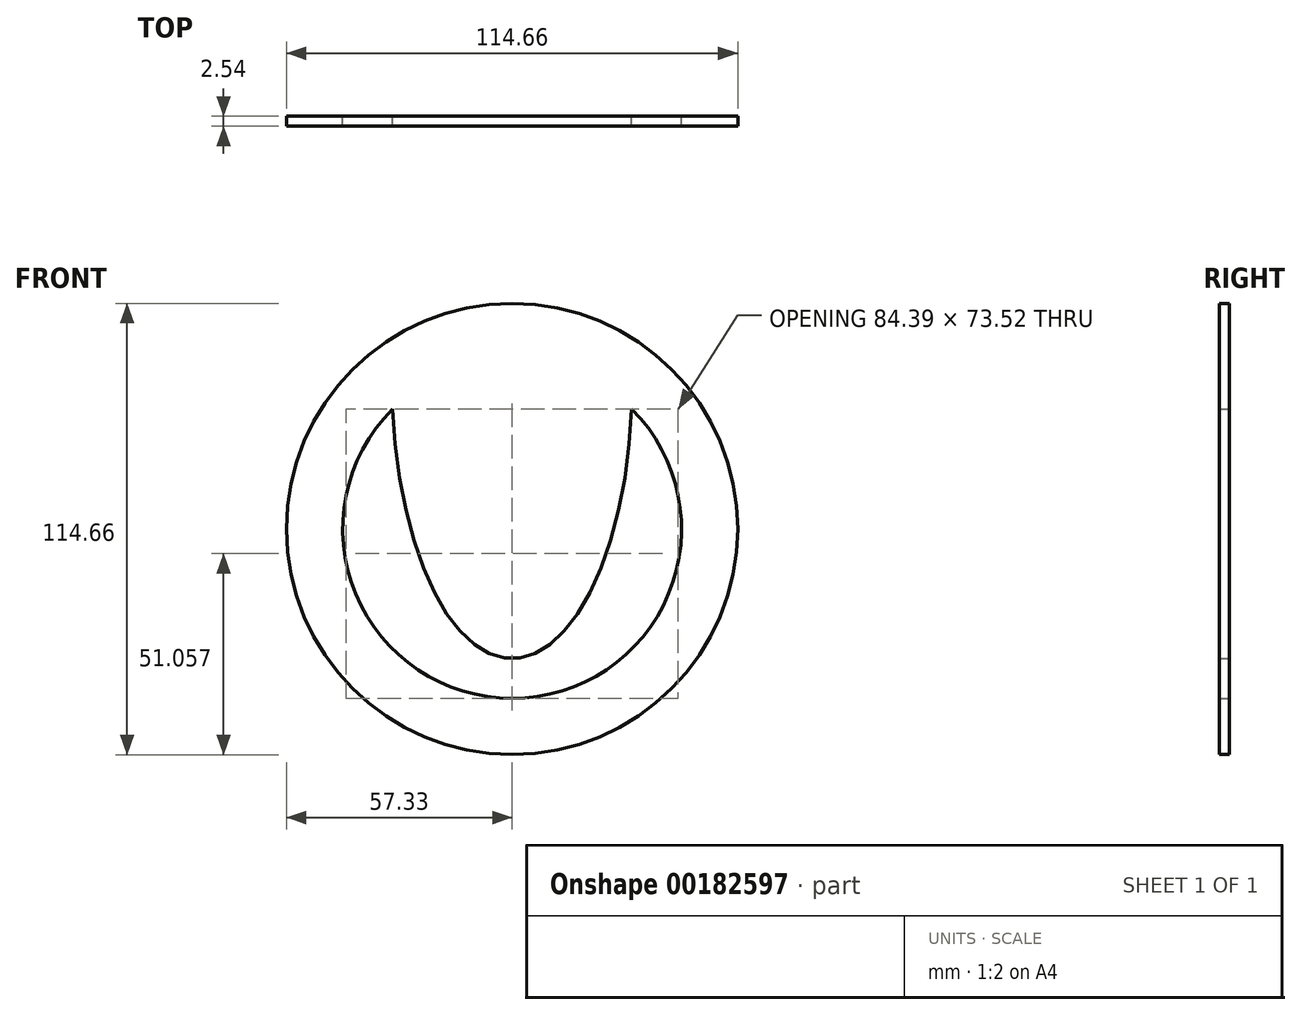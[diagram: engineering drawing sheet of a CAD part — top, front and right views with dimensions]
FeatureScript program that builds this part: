
annotation { "Feature Type Name" : "Feature", "Feature Type Description" : "" }
export const myFeature = defineFeature(function(context is Context, id is Id, definition is map)
    precondition{}
    {
        {
            var Q0;
            Q0=qCreatedBy(makeId("Front.planeOp"),FACE);
            var sketch = newSketch(context, id + "F0", { "sketchPlane" : qUnion([Q0])});
            skCircle(sketch, "E0", {"center": v(0, 0) * mm, "radius": 43.03 * mm});
            skEllipticalArc(sketch, "E1", {});
            skCircle(sketch, "E2", {"center": v(0, 0) * mm, "radius": 57.33 * mm});
            const initialGuessF0  = {"E1": [0, 0.03760869428515434, 0, -1, 0.07045922800898552, 0.030526821522281266, 4.813650019561177, 1.4695352876184096]};
            skSetInitialGuess(sketch, initialGuessF0);
            skSolve(sketch);
        }
        {
            var Q0;
            Q0 = qSketchRegion(id + "F0", true);
            var Q1;
            {var subQ0=sQuery(id+"F0.wireOp",EDGE,"E1");Q1=makeQuery(id+"F0.imprint","IMPRINT",FACE,{"disambiguationData":[TD([[makeQuery(id+"F0.imprint","IMPRINT",EDGE,{"derivedFrom":subQ0}),1.0]])]});}
            extrude(context, id + "F1", {"entities" : qUnion([Q0, Q1]), "depth" : 2.54 * mm});
        }
    });
